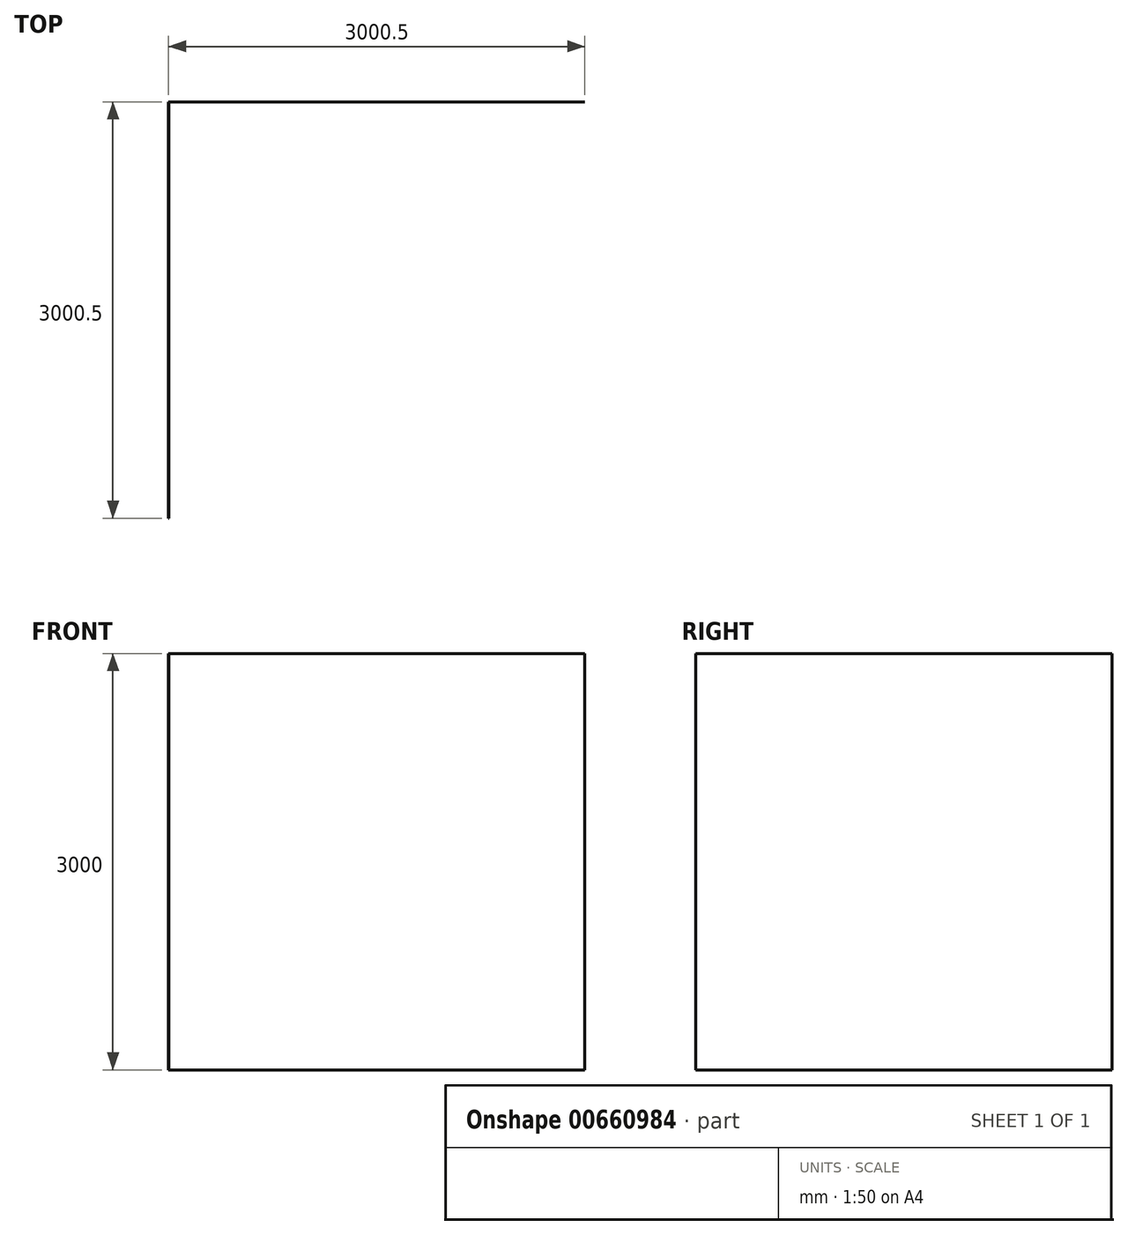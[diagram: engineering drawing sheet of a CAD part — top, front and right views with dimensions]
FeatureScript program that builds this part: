
annotation { "Feature Type Name" : "Feature", "Feature Type Description" : "" }
export const myFeature = defineFeature(function(context is Context, id is Id, definition is map)
    precondition{}
    {
        {
            var Q0;
            Q0=qCreatedBy(makeId("Top.planeOp"),FACE);
            var sketch = newSketch(context, id + "F0", { "sketchPlane" : qUnion([Q0])});
            skLineSegment(sketch, "E0.bottom", {"start": v(0, 0) * mm, "end": v(3000, 0) * mm});
            skLineSegment(sketch, "E0.top", {"start": v(0, 0.5) * mm, "end": v(3000, 0.5) * mm});
            skLineSegment(sketch, "E0.left", {"start": v(0, 0) * mm, "end": v(0, 0.5) * mm});
            skLineSegment(sketch, "E0.right", {"start": v(3000, 0) * mm, "end": v(3000, 0.5) * mm});
            skLineSegment(sketch, "E1.bottom", {"start": v(0, 0) * mm, "end": v(-0.5, 0) * mm});
            skLineSegment(sketch, "E1.top", {"start": v(0, -3000) * mm, "end": v(-0.5, -3000) * mm});
            skLineSegment(sketch, "E1.left", {"start": v(0, 0) * mm, "end": v(0, -3000) * mm});
            skLineSegment(sketch, "E1.right", {"start": v(-0.5, 0) * mm, "end": v(-0.5, -3000) * mm});
            skSolve(sketch);
        }
        {
            var Q0;
            Q0=makeQuery(id+"F0.imprint","IMPRINT",FACE,{"disambiguationData":[TD([[makeQuery(id+"F0.imprint","IMPRINT",EDGE,{"derivedFrom":sQuery(id+"F0.wireOp",EDGE,"E0.bottom")}),1.0]])]});
            var Q1;
            Q1=makeQuery(id+"F0.imprint","IMPRINT",FACE,{"disambiguationData":[TD([[makeQuery(id+"F0.imprint","IMPRINT",EDGE,{"derivedFrom":sQuery(id+"F0.wireOp",EDGE,"E1.bottom")}),1.0]])]});
            extrude(context, id + "F1", {"entities" : qUnion([Q0, Q1]), "depth" : 3000 * mm, "offsetDistance" : 25 * mm});
        }
    });
